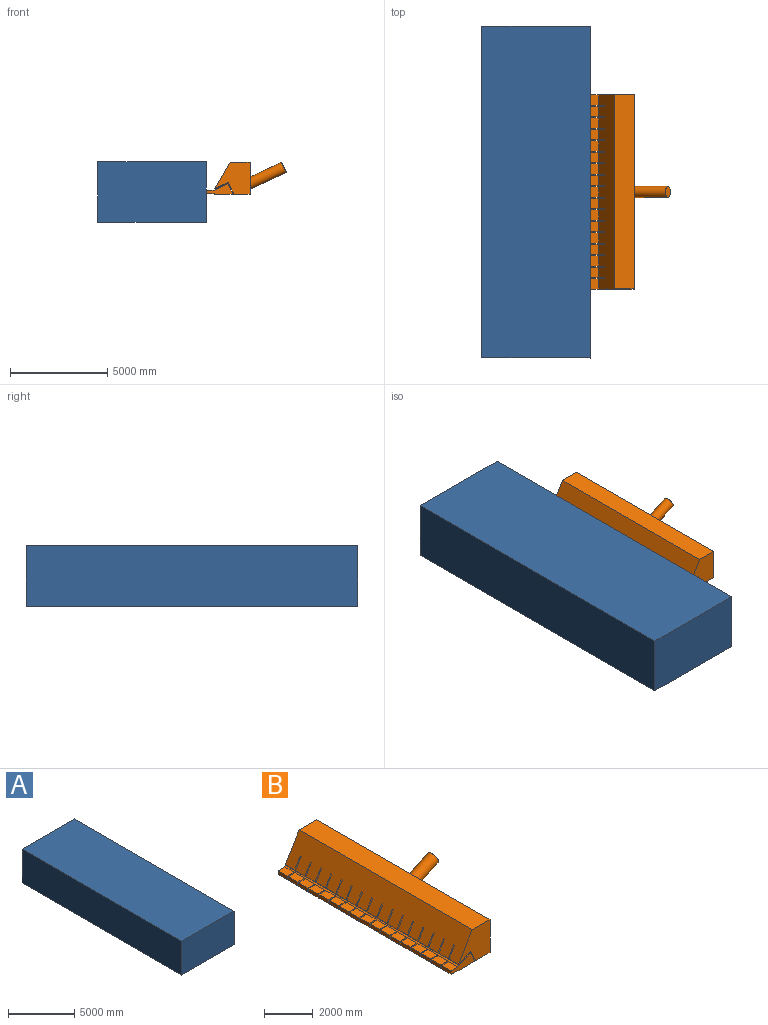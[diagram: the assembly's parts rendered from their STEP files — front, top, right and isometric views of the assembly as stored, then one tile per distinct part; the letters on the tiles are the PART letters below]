
ASSEMBLY  parts=2 mates=1
PART A: 6 faces, bbox 5600x17102.8x3131.8 mm
  f0: plane 5600x3131.8mm, normal (0,1,0), area 17538052.5mm2, adj f1,f3,f4,f5
  f1: plane 17102.78x5600mm, normal (0,0,1), area 95775550.1mm2, adj f0,f2,f4,f5
  f2: plane 5600x3131.8mm, normal (0,-1,0), area 17538052.5mm2, adj f1,f3,f4,f5
  f3: plane 17102.78x5600mm, normal (0,0,-1), area 95775550.1mm2, adj f0,f2,f4,f5
  f4: plane 17102.78x3131.8mm, normal (1,0,0), area 53562392.3mm2, adj f0,f1,f2,f3
  f5: plane 17102.78x3131.8mm, normal (-1,0,0), area 53562392.3mm2, adj f0,f1,f2,f3
PART B: 333 faces, bbox 4166.6x10055.9x1705.6 mm
  f0: plane 540x397.5mm, normal (0,0,1), area 214650.5mm2, adj f16,f38,f85,f86
  f1: plane 540x397.5mm, normal (0,0,1), area 214650.5mm2, adj f17,f38,f82,f83
  f2: plane 540x397.5mm, normal (0,0,1), area 214650.5mm2, adj f18,f38,f79,f80
  f3: plane 540x397.5mm, normal (0,0,1), area 214650.5mm2, adj f19,f38,f76,f77
  f4: plane 540x397.5mm, normal (0,0,1), area 214650.5mm2, adj f20,f38,f73,f74
  f5: plane 540x397.5mm, normal (0,0,1), area 214650.5mm2, adj f21,f38,f70,f71
  f6: plane 540x397.5mm, normal (0,0,1), area 214650.5mm2, adj f22,f38,f55,f68
  f7: plane 540x397.5mm, normal (0,0,1), area 214650.5mm2, adj f23,f38,f64,f65
  f8: plane 540x397.5mm, normal (0,0,1), area 214650.5mm2, adj f24,f38,f61,f62
  f9: plane 540x397.5mm, normal (0,0,1), area 214650.5mm2, adj f25,f38,f58,f59
  f10: plane 540x397.5mm, normal (0,0,1), area 214650.5mm2, adj f26,f38,f46,f56
  f11: plane 540x397.5mm, normal (0,0,1), area 214650.5mm2, adj f27,f38,f42,f53
  f12: plane 540x397.5mm, normal (0,0,1), area 214650.5mm2, adj f28,f38,f39,f50
  f13: plane 540x397.5mm, normal (0,0,1), area 214650.5mm2, adj f29,f38,f47,f52
  f14: plane 540x397.5mm, normal (0,0,1), area 214650.5mm2, adj f30,f38,f44,f49
  f15: plane 540x397.5mm, normal (0,0,1), area 214650.5mm2, adj f31,f38,f43,f67
  f16: plane 540x180.58mm, normal (-1,0,0), area 97510.9mm2, adj f0,f32,f85,f86
  f17: plane 540x180.58mm, normal (-1,0,0), area 97510.9mm2, adj f1,f32,f82,f83
  f18: plane 540x180.58mm, normal (-1,0,0), area 97510.9mm2, adj f2,f32,f79,f80
  f19: plane 540x180.58mm, normal (-1,0,0), area 97510.9mm2, adj f3,f32,f76,f77
  f20: plane 540x180.58mm, normal (-1,0,0), area 97510.9mm2, adj f4,f32,f73,f74
  f21: plane 540x180.58mm, normal (-1,0,0), area 97510.9mm2, adj f5,f32,f70,f71
  f22: plane 540x180.58mm, normal (-1,0,0), area 97510.9mm2, adj f6,f32,f55,f68
  f23: plane 540x180.58mm, normal (-1,0,0), area 97510.9mm2, adj f7,f32,f64,f65
  f24: plane 540x180.58mm, normal (-1,0,0), area 97510.9mm2, adj f8,f32,f61,f62
  f25: plane 540x180.58mm, normal (-1,0,0), area 97510.9mm2, adj f9,f32,f58,f59
  f26: plane 540x180.58mm, normal (-1,0,0), area 97510.9mm2, adj f10,f32,f46,f56
  f27: plane 540x180.58mm, normal (-1,0,0), area 97510.9mm2, adj f11,f32,f42,f53
  f28: plane 540x180.58mm, normal (-1,0,0), area 97510.9mm2, adj f12,f32,f39,f50
  f29: plane 540x180.58mm, normal (-1,0,0), area 97510.9mm2, adj f13,f32,f47,f52
  f30: plane 540x180.58mm, normal (-1,0,0), area 97510.9mm2, adj f14,f32,f44,f49
  f31: plane 540x180.58mm, normal (-1,0,0), area 97510.9mm2, adj f15,f32,f43,f67
  f32: plane 10000x398.52mm, normal (0,0,-1), area 3659198.5mm2, adj f16,f17,f18,f19,f20,f21,f22,f23
  f33: plane 540x397.5mm, normal (0,0,1), area 214650.5mm2, adj f34,f38,f40,f88
  f34: plane 540x180.58mm, normal (-1,0,0), area 97510.9mm2, adj f32,f33,f40,f88
  f35: plane 10000x24.82mm, normal (-1,0,0), area 248229.5mm2, adj f32,f36,f39,f40
  f36: plane 10000x976.6mm, normal (0,0,-1), area 9765991mm2, adj f35,f37,f39,f40
  f37: plane 10000x555.14mm, normal (0.89,0,0.45), area 6206617.3mm2, adj f36,f38,f39,f40
  f38: plane 10000x699.89mm, normal (-0.45,0,0.89), area 5947466.5mm2, adj f0,f1,f2,f3,f4,f5,f6,f7
  f39: plane 1375.12x555.14mm, normal (0,-1,0), area 414848.3mm2, adj f12,f28,f32,f35,f36,f37,f38
  f40: plane 1375.12x555.14mm, normal (0,1,0), area 414848.3mm2, adj f32,f33,f34,f35,f36,f37,f38
  f41: plane 180.37x51.25mm, normal (-1,0,0), area 9243.8mm2, adj f32,f38,f42,f43
  f42: plane 397.66x180.58mm, normal (0,-1,0), area 71742.9mm2, adj f11,f27,f32,f41
  f43: plane 397.66x180.58mm, normal (0,1,0), area 71742.9mm2, adj f15,f31,f32,f41
  f44: plane 397.66x180.58mm, normal (0,1,0), area 71742.9mm2, adj f14,f30,f32,f45
  f45: plane 180.37x51.25mm, normal (-1,0,0), area 9243.8mm2, adj f32,f38,f44,f46
  f46: plane 397.66x180.58mm, normal (0,-1,0), area 71742.9mm2, adj f10,f26,f32,f45
  f47: plane 397.66x180.58mm, normal (0,1,0), area 71742.9mm2, adj f13,f29,f32,f48
  f48: plane 180.37x51.25mm, normal (-1,0,0), area 9243.8mm2, adj f32,f38,f47,f49
  f49: plane 397.66x180.58mm, normal (0,-1,0), area 71742.9mm2, adj f14,f30,f32,f48
  f50: plane 397.66x180.58mm, normal (0,1,0), area 71742.9mm2, adj f12,f28,f32,f51
  f51: plane 180.37x51.25mm, normal (-1,0,0), area 9243.8mm2, adj f32,f38,f50,f52
  f52: plane 397.66x180.58mm, normal (0,-1,0), area 71742.9mm2, adj f13,f29,f32,f51
  f53: plane 397.66x180.58mm, normal (0,1,0), area 71742.9mm2, adj f11,f27,f32,f54
  f54: plane 180.37x51.25mm, normal (-1,0,0), area 9243.8mm2, adj f32,f38,f53,f55
  f55: plane 397.66x180.58mm, normal (0,-1,0), area 71742.9mm2, adj f6,f22,f32,f54
  f56: plane 397.66x180.58mm, normal (0,1,0), area 71742.9mm2, adj f10,f26,f32,f57
  f57: plane 180.37x51.25mm, normal (-1,0,0), area 9243.8mm2, adj f32,f38,f56,f58
  f58: plane 397.66x180.58mm, normal (0,-1,0), area 71742.9mm2, adj f9,f25,f32,f57
  f59: plane 397.66x180.58mm, normal (0,1,0), area 71742.9mm2, adj f9,f25,f32,f60
  f60: plane 180.37x51.25mm, normal (-1,0,0), area 9243.8mm2, adj f32,f38,f59,f61
  f61: plane 397.66x180.58mm, normal (0,-1,0), area 71742.9mm2, adj f8,f24,f32,f60
  f62: plane 397.66x180.58mm, normal (0,1,0), area 71742.9mm2, adj f8,f24,f32,f63
  f63: plane 180.37x51.25mm, normal (-1,0,0), area 9243.8mm2, adj f32,f38,f62,f64
  f64: plane 397.66x180.58mm, normal (0,-1,0), area 71742.9mm2, adj f7,f23,f32,f63
  f65: plane 397.66x180.58mm, normal (0,1,0), area 71742.9mm2, adj f7,f23,f32,f66
  f66: plane 180.37x51.25mm, normal (-1,0,0), area 9243.8mm2, adj f32,f38,f65,f67
  f67: plane 397.66x180.58mm, normal (0,-1,0), area 71742.9mm2, adj f15,f31,f32,f66
  f68: plane 397.66x180.58mm, normal (0,1,0), area 71742.9mm2, adj f6,f22,f32,f69
  f69: plane 180.37x51.25mm, normal (-1,0,0), area 9243.8mm2, adj f32,f38,f68,f70
  f70: plane 397.66x180.58mm, normal (0,-1,0), area 71742.9mm2, adj f5,f21,f32,f69
  f71: plane 397.66x180.58mm, normal (0,1,0), area 71742.9mm2, adj f5,f21,f32,f72
  f72: plane 180.37x51.25mm, normal (-1,0,0), area 9243.8mm2, adj f32,f38,f71,f73
  f73: plane 397.66x180.58mm, normal (0,-1,0), area 71742.9mm2, adj f4,f20,f32,f72
  f74: plane 397.66x180.58mm, normal (0,1,0), area 71742.9mm2, adj f4,f20,f32,f75
  f75: plane 180.37x51.25mm, normal (-1,0,0), area 9243.8mm2, adj f32,f38,f74,f76
  f76: plane 397.66x180.58mm, normal (0,-1,0), area 71742.9mm2, adj f3,f19,f32,f75
  f77: plane 397.66x180.58mm, normal (0,1,0), area 71742.9mm2, adj f3,f19,f32,f78
  f78: plane 180.37x51.25mm, normal (-1,0,0), area 9243.8mm2, adj f32,f38,f77,f79
  f79: plane 397.66x180.58mm, normal (0,-1,0), area 71742.9mm2, adj f2,f18,f32,f78
  f80: plane 397.66x180.58mm, normal (0,1,0), area 71742.9mm2, adj f2,f18,f32,f81
  f81: plane 180.37x51.25mm, normal (-1,0,0), area 9243.8mm2, adj f32,f38,f80,f82
  f82: plane 397.66x180.58mm, normal (0,-1,0), area 71742.9mm2, adj f1,f17,f32,f81
  f83: plane 397.66x180.58mm, normal (0,1,0), area 71742.9mm2, adj f1,f17,f32,f84
  f84: plane 180.37x51.25mm, normal (-1,0,0), area 9243.8mm2, adj f32,f38,f83,f85
  f85: plane 397.66x180.58mm, normal (0,-1,0), area 71742.9mm2, adj f0,f16,f32,f84
  f86: plane 397.66x180.58mm, normal (0,1,0), area 71742.9mm2, adj f0,f16,f32,f87
  f87: plane 180.37x51.25mm, normal (-1,0,0), area 9243.8mm2, adj f32,f38,f86,f88
  f88: plane 397.66x180.58mm, normal (0,-1,0), area 71742.9mm2, adj f32,f33,f34,f87
  f89: plane 540x25.23mm, normal (-0.93,0,-0.36), area 14632mm2, adj f105,f123,f131,f177
  f90: plane 540x25.23mm, normal (-0.93,0,-0.36), area 14632mm2, adj f106,f123,f169,f174
  f91: plane 540x25.23mm, normal (-0.93,0,-0.36), area 14632mm2, adj f107,f123,f166,f171
  f92: plane 540x25.23mm, normal (-0.93,0,-0.36), area 14632mm2, adj f108,f123,f163,f168
  f93: plane 540x25.23mm, normal (-0.93,0,-0.36), area 14632mm2, adj f109,f123,f160,f165
  f94: plane 540x25.23mm, normal (-0.93,0,-0.36), area 14632mm2, adj f110,f123,f157,f162
  f95: plane 540x25.23mm, normal (-0.93,0,-0.36), area 14632mm2, adj f111,f123,f154,f159
  f96: plane 540x25.23mm, normal (-0.93,0,-0.36), area 14632mm2, adj f112,f123,f151,f156
  f97: plane 540x25.23mm, normal (-0.93,0,-0.36), area 14632mm2, adj f113,f123,f129,f153
  f98: plane 540x25.23mm, normal (-0.93,0,-0.36), area 14632mm2, adj f114,f123,f150,f175
  f99: plane 540x25.23mm, normal (-0.93,0,-0.36), area 14632mm2, adj f115,f123,f147,f148
  f100: plane 540x25.23mm, normal (-0.93,0,-0.36), area 14632mm2, adj f116,f123,f144,f145
  f101: plane 540x25.23mm, normal (-0.93,0,-0.36), area 14632mm2, adj f117,f123,f141,f142
  f102: plane 540x25.23mm, normal (-0.93,0,-0.36), area 14632mm2, adj f118,f123,f138,f139
  f103: plane 540x25.23mm, normal (-0.93,0,-0.36), area 14632mm2, adj f119,f123,f135,f136
  f104: plane 540x25.23mm, normal (-0.93,0,-0.36), area 14632mm2, adj f120,f123,f132,f172
  f105: plane 684.4x540mm, normal (0.45,0,-0.89), area 302751.2mm2, adj f89,f126,f131,f177,f187,f188,f189,f190
  f106: plane 684.4x540mm, normal (0.45,0,-0.89), area 302751.2mm2, adj f90,f126,f169,f174,f257,f258,f259,f260
  f107: plane 684.4x540mm, normal (0.45,0,-0.89), area 302751.2mm2, adj f91,f126,f166,f171,f248,f249,f250,f251
  f108: plane 684.4x540mm, normal (0.45,0,-0.89), area 302751.2mm2, adj f92,f126,f163,f168,f239,f240,f241,f242
  f109: plane 684.4x540mm, normal (0.45,0,-0.89), area 302751.2mm2, adj f93,f126,f160,f165,f230,f231,f232,f233
  f110: plane 684.4x540mm, normal (0.45,0,-0.89), area 302751.2mm2, adj f94,f126,f157,f162,f221,f222,f223,f224
  f111: plane 684.4x540mm, normal (0.45,0,-0.89), area 302751.2mm2, adj f95,f126,f154,f159,f210,f213,f214,f215
  f112: plane 684.4x540mm, normal (0.45,0,-0.89), area 302751.2mm2, adj f96,f126,f151,f156,f203,f204,f205,f206
  f113: plane 684.4x540mm, normal (0.45,0,-0.89), area 302751.2mm2, adj f97,f126,f129,f153,f196,f197,f198,f199
  f114: plane 684.4x540mm, normal (0.45,0,-0.89), area 302751.2mm2, adj f98,f126,f150,f175,f266,f267,f268,f269
  f115: plane 684.4x540mm, normal (0.45,0,-0.89), area 302751.2mm2, adj f99,f126,f147,f148,f275,f276,f277,f278
  f116: plane 684.4x540mm, normal (0.45,0,-0.89), area 302751.2mm2, adj f100,f126,f144,f145,f284,f285,f286,f287
  f117: plane 684.4x540mm, normal (0.45,0,-0.89), area 302751.2mm2, adj f101,f126,f141,f142,f288,f294,f295,f296
  f118: plane 684.4x540mm, normal (0.45,0,-0.89), area 302751.2mm2, adj f102,f126,f138,f139,f302,f303,f304,f305
  f119: plane 684.4x540mm, normal (0.45,0,-0.89), area 302751.2mm2, adj f103,f126,f135,f136,f311,f312,f313,f314
  f120: plane 684.4x540mm, normal (0.45,0,-0.89), area 302751.2mm2, adj f104,f126,f132,f172,f178,f179,f180,f181
  f121: plane 10055.9x1700.9mm, normal (1,0,0), area 16168489.7mm2, adj f122,f127,f128,f129,f331
  f122: plane 10000x1029.08mm, normal (0,0,1), area 10290780.5mm2, adj f121,f123,f128,f129
  f123: plane 10000x1346.2mm, normal (-0.86,0,0.51), area 15132204mm2, adj f89,f90,f91,f92,f93,f94,f95,f96
  f124: plane 540x25.23mm, normal (-0.93,0,-0.36), area 14632mm2, adj f123,f125,f128,f133
  f125: plane 684.4x540mm, normal (0.45,0,-0.89), area 302751.2mm2, adj f124,f126,f128,f133,f320,f321,f322,f323
  f126: plane 10000x616.66mm, normal (-0.89,0,-0.45), area 6894431.3mm2, adj f105,f106,f107,f108,f109,f110,f111,f112
  f127: plane 10000x823.79mm, normal (0,0,-1), area 8237894.6mm2, adj f121,f126,f128,f129
  f128: plane 1826.39x1645.89mm, normal (0,-1,0), area 2066070.7mm2, adj f121,f122,f123,f124,f125,f126,f127
  f129: plane 1826.39x1645.89mm, normal (0,1,0), area 2066070.7mm2, adj f97,f113,f121,f122,f123,f126,f127
  f130: plane 375x222.1mm, normal (-0.51,0,-0.86), area 22336.6mm2, adj f123,f126,f131,f132
  f131: plane 694.27x564.3mm, normal (0,1,0), area 146854.6mm2, adj f89,f105,f123,f130
  f132: plane 694.27x564.3mm, normal (0,-1,0), area 146854.6mm2, adj f104,f120,f123,f130
  f133: plane 694.27x564.3mm, normal (0,1,0), area 146854.6mm2, adj f123,f124,f125,f134
  f134: plane 375x222.1mm, normal (-0.51,0,-0.86), area 22336.6mm2, adj f123,f126,f133,f135
  f135: plane 694.27x564.3mm, normal (0,-1,0), area 146854.6mm2, adj f103,f119,f123,f134
  f136: plane 694.27x564.3mm, normal (0,1,0), area 146854.6mm2, adj f103,f119,f123,f137
  f137: plane 375x222.1mm, normal (-0.51,0,-0.86), area 22336.6mm2, adj f123,f126,f136,f138
  f138: plane 694.27x564.3mm, normal (0,-1,0), area 146854.6mm2, adj f102,f118,f123,f137
  f139: plane 694.27x564.3mm, normal (0,1,0), area 146854.6mm2, adj f102,f118,f123,f140
  f140: plane 375x222.1mm, normal (-0.51,0,-0.86), area 22336.6mm2, adj f123,f126,f139,f141
  f141: plane 694.27x564.3mm, normal (0,-1,0), area 146854.6mm2, adj f101,f117,f123,f140
  f142: plane 694.27x564.3mm, normal (0,1,0), area 146854.6mm2, adj f101,f117,f123,f143
  f143: plane 375x222.1mm, normal (-0.51,0,-0.86), area 22336.6mm2, adj f123,f126,f142,f144
  f144: plane 694.27x564.3mm, normal (0,-1,0), area 146854.6mm2, adj f100,f116,f123,f143
  f145: plane 694.27x564.3mm, normal (0,1,0), area 146854.6mm2, adj f100,f116,f123,f146
  f146: plane 375x222.1mm, normal (-0.51,0,-0.86), area 22336.6mm2, adj f123,f126,f145,f147
  f147: plane 694.27x564.3mm, normal (0,-1,0), area 146854.6mm2, adj f99,f115,f123,f146
  f148: plane 694.27x564.3mm, normal (0,1,0), area 146854.6mm2, adj f99,f115,f123,f149
  f149: plane 375x222.1mm, normal (-0.51,0,-0.86), area 22336.6mm2, adj f123,f126,f148,f150
  f150: plane 694.27x564.3mm, normal (0,-1,0), area 146854.6mm2, adj f98,f114,f123,f149
  f151: plane 694.27x564.3mm, normal (0,1,0), area 146854.6mm2, adj f96,f112,f123,f152
  f152: plane 375x222.1mm, normal (-0.51,0,-0.86), area 22336.6mm2, adj f123,f126,f151,f153
  f153: plane 694.27x564.3mm, normal (0,-1,0), area 146854.6mm2, adj f97,f113,f123,f152
  f154: plane 694.27x564.3mm, normal (0,1,0), area 146854.6mm2, adj f95,f111,f123,f155
  f155: plane 375x222.1mm, normal (-0.51,0,-0.86), area 22336.6mm2, adj f123,f126,f154,f156
  f156: plane 694.27x564.3mm, normal (0,-1,0), area 146854.6mm2, adj f96,f112,f123,f155
  f157: plane 694.27x564.3mm, normal (0,1,0), area 146854.6mm2, adj f94,f110,f123,f158
  f158: plane 375x222.1mm, normal (-0.51,0,-0.86), area 22336.6mm2, adj f123,f126,f157,f159
  f159: plane 694.27x564.3mm, normal (0,-1,0), area 146854.6mm2, adj f95,f111,f123,f158
  f160: plane 694.27x564.3mm, normal (0,1,0), area 146854.6mm2, adj f93,f109,f123,f161
  f161: plane 375x222.1mm, normal (-0.51,0,-0.86), area 22336.6mm2, adj f123,f126,f160,f162
  f162: plane 694.27x564.3mm, normal (0,-1,0), area 146854.6mm2, adj f94,f110,f123,f161
  f163: plane 694.27x564.3mm, normal (0,1,0), area 146854.6mm2, adj f92,f108,f123,f164
  f164: plane 375x222.1mm, normal (-0.51,0,-0.86), area 22336.6mm2, adj f123,f126,f163,f165
  f165: plane 694.27x564.3mm, normal (0,-1,0), area 146854.6mm2, adj f93,f109,f123,f164
  f166: plane 694.27x564.3mm, normal (0,1,0), area 146854.6mm2, adj f91,f107,f123,f167
  f167: plane 375x222.1mm, normal (-0.51,0,-0.86), area 22336.6mm2, adj f123,f126,f166,f168
  f168: plane 694.27x564.3mm, normal (0,-1,0), area 146854.6mm2, adj f92,f108,f123,f167
  f169: plane 694.27x564.3mm, normal (0,1,0), area 146854.6mm2, adj f90,f106,f123,f170
  f170: plane 375x222.1mm, normal (-0.51,0,-0.86), area 22336.6mm2, adj f123,f126,f169,f171
  f171: plane 694.27x564.3mm, normal (0,-1,0), area 146854.6mm2, adj f91,f107,f123,f170
  f172: plane 694.27x564.3mm, normal (0,1,0), area 146854.6mm2, adj f104,f120,f123,f173
  f173: plane 375x222.1mm, normal (-0.51,0,-0.86), area 22336.6mm2, adj f123,f126,f172,f174
  f174: plane 694.27x564.3mm, normal (0,-1,0), area 146854.6mm2, adj f90,f106,f123,f173
  f175: plane 694.27x564.3mm, normal (0,1,0), area 146854.6mm2, adj f98,f114,f123,f176
  f176: plane 375x222.1mm, normal (-0.51,0,-0.86), area 22336.6mm2, adj f123,f126,f175,f177
  f177: plane 694.27x564.3mm, normal (0,-1,0), area 146854.6mm2, adj f89,f105,f123,f176
  f178: cylinder r=62.5mm len=132.32mm, axis (0.45,0,-0.89), area 18015.8mm2, adj f38,f120
  f179: cylinder r=62.5mm len=132.32mm, axis (0.45,0,-0.89), area 18015.8mm2, adj f38,f120
  f180: cylinder r=62.5mm len=132.32mm, axis (0.45,0,-0.89), area 18015.8mm2, adj f38,f120
  f181: cylinder r=62.5mm len=132.32mm, axis (0.45,0,-0.89), area 18015.8mm2, adj f38,f120
  f182: cylinder r=62.5mm len=132.32mm, axis (0.45,0,-0.89), area 18015.8mm2, adj f38,f120
  f183: cylinder r=62.5mm len=132.32mm, axis (0.45,0,-0.89), area 18015.8mm2, adj f38,f120
  f184: cylinder r=62.5mm len=132.32mm, axis (0.45,0,-0.89), area 18015.8mm2, adj f38,f120
  f185: cylinder r=62.5mm len=132.32mm, axis (0.45,0,-0.89), area 18015.8mm2, adj f38,f120
  f186: cylinder r=62.5mm len=132.32mm, axis (0.45,0,-0.89), area 18015.8mm2, adj f38,f120
  f187: cylinder r=62.5mm len=132.32mm, axis (0.45,0,-0.89), area 18015.8mm2, adj f38,f105
  f188: cylinder r=62.5mm len=132.32mm, axis (0.45,0,-0.89), area 18015.8mm2, adj f38,f105
  f189: cylinder r=62.5mm len=132.32mm, axis (0.45,0,-0.89), area 18015.8mm2, adj f38,f105
  f190: cylinder r=62.5mm len=132.32mm, axis (0.45,0,-0.89), area 18015.8mm2, adj f38,f105
  f191: cylinder r=62.5mm len=132.32mm, axis (0.45,0,-0.89), area 18015.8mm2, adj f38,f105
  f192: cylinder r=62.5mm len=132.32mm, axis (0.45,0,-0.89), area 18015.8mm2, adj f38,f105
  f193: cylinder r=62.5mm len=132.32mm, axis (0.45,0,-0.89), area 18015.8mm2, adj f38,f105
  f194: cylinder r=62.5mm len=132.32mm, axis (0.45,0,-0.89), area 18015.8mm2, adj f38,f105
  f195: cylinder r=62.5mm len=132.32mm, axis (0.45,0,-0.89), area 18015.8mm2, adj f38,f105
  f196: cylinder r=62.5mm len=132.32mm, axis (0.45,0,-0.89), area 18015.8mm2, adj f38,f113
  f197: cylinder r=62.5mm len=132.32mm, axis (0.45,0,-0.89), area 18015.8mm2, adj f38,f113
  f198: cylinder r=62.5mm len=132.32mm, axis (0.45,0,-0.89), area 18015.8mm2, adj f38,f113
  f199: cylinder r=62.5mm len=132.32mm, axis (0.45,0,-0.89), area 18015.8mm2, adj f38,f113
  f200: cylinder r=62.5mm len=132.32mm, axis (0.45,0,-0.89), area 18015.8mm2, adj f38,f113
  f201: cylinder r=62.5mm len=132.32mm, axis (0.45,0,-0.89), area 18015.8mm2, adj f38,f113
  f202: cylinder r=62.5mm len=132.32mm, axis (0.45,0,-0.89), area 18015.8mm2, adj f38,f113
  f203: cylinder r=62.5mm len=132.32mm, axis (0.45,0,-0.89), area 18015.8mm2, adj f38,f112
  f204: cylinder r=62.5mm len=132.32mm, axis (0.45,0,-0.89), area 18015.8mm2, adj f38,f112
  f205: cylinder r=62.5mm len=132.32mm, axis (0.45,0,-0.89), area 18015.8mm2, adj f38,f112
  f206: cylinder r=62.5mm len=132.32mm, axis (0.45,0,-0.89), area 18015.8mm2, adj f38,f112
  f207: cylinder r=62.5mm len=132.32mm, axis (0.45,0,-0.89), area 18015.8mm2, adj f38,f112
  f208: cylinder r=62.5mm len=132.32mm, axis (0.45,0,-0.89), area 18015.8mm2, adj f38,f112
  f209: cylinder r=62.5mm len=132.32mm, axis (0.45,0,-0.89), area 18015.8mm2, adj f38,f112
  f210: cylinder r=62.5mm len=132.32mm, axis (0.45,0,-0.89), area 18015.8mm2, adj f38,f111
  f211: cylinder r=62.5mm len=132.32mm, axis (0.45,0,-0.89), area 18015.8mm2, adj f38,f112
  f212: cylinder r=62.5mm len=132.32mm, axis (0.45,0,-0.89), area 18015.8mm2, adj f38,f112
  f213: cylinder r=62.5mm len=132.32mm, axis (0.45,0,-0.89), area 18015.8mm2, adj f38,f111
  f214: cylinder r=62.5mm len=132.32mm, axis (0.45,0,-0.89), area 18015.8mm2, adj f38,f111
  f215: cylinder r=62.5mm len=132.32mm, axis (0.45,0,-0.89), area 18015.8mm2, adj f38,f111
  f216: cylinder r=62.5mm len=132.32mm, axis (0.45,0,-0.89), area 18015.8mm2, adj f38,f111
  f217: cylinder r=62.5mm len=132.32mm, axis (0.45,0,-0.89), area 18015.8mm2, adj f38,f111
  f218: cylinder r=62.5mm len=132.32mm, axis (0.45,0,-0.89), area 18015.8mm2, adj f38,f111
  f219: cylinder r=62.5mm len=132.32mm, axis (0.45,0,-0.89), area 18015.8mm2, adj f38,f111
  f220: cylinder r=62.5mm len=132.32mm, axis (0.45,0,-0.89), area 18015.8mm2, adj f38,f111
  f221: cylinder r=62.5mm len=132.32mm, axis (0.45,0,-0.89), area 18015.8mm2, adj f38,f110
  f222: cylinder r=62.5mm len=132.32mm, axis (0.45,0,-0.89), area 18015.8mm2, adj f38,f110
  f223: cylinder r=62.5mm len=132.32mm, axis (0.45,0,-0.89), area 18015.8mm2, adj f38,f110
  f224: cylinder r=62.5mm len=132.32mm, axis (0.45,0,-0.89), area 18015.8mm2, adj f38,f110
  f225: cylinder r=62.5mm len=132.32mm, axis (0.45,0,-0.89), area 18015.8mm2, adj f38,f110
  f226: cylinder r=62.5mm len=132.32mm, axis (0.45,0,-0.89), area 18015.8mm2, adj f38,f110
  f227: cylinder r=62.5mm len=132.32mm, axis (0.45,0,-0.89), area 18015.8mm2, adj f38,f110
  f228: cylinder r=62.5mm len=132.32mm, axis (0.45,0,-0.89), area 18015.8mm2, adj f38,f110
  f229: cylinder r=62.5mm len=132.32mm, axis (0.45,0,-0.89), area 18015.8mm2, adj f38,f110
  f230: cylinder r=62.5mm len=132.32mm, axis (0.45,0,-0.89), area 18015.8mm2, adj f38,f109
  f231: cylinder r=62.5mm len=132.32mm, axis (0.45,0,-0.89), area 18015.8mm2, adj f38,f109
  f232: cylinder r=62.5mm len=132.32mm, axis (0.45,0,-0.89), area 18015.8mm2, adj f38,f109
  f233: cylinder r=62.5mm len=132.32mm, axis (0.45,0,-0.89), area 18015.8mm2, adj f38,f109
  f234: cylinder r=62.5mm len=132.32mm, axis (0.45,0,-0.89), area 18015.8mm2, adj f38,f109
  f235: cylinder r=62.5mm len=132.32mm, axis (0.45,0,-0.89), area 18015.8mm2, adj f38,f109
  f236: cylinder r=62.5mm len=132.32mm, axis (0.45,0,-0.89), area 18015.8mm2, adj f38,f109
  f237: cylinder r=62.5mm len=132.32mm, axis (0.45,0,-0.89), area 18015.8mm2, adj f38,f109
  f238: cylinder r=62.5mm len=132.32mm, axis (0.45,0,-0.89), area 18015.8mm2, adj f38,f109
  f239: cylinder r=62.5mm len=132.32mm, axis (0.45,0,-0.89), area 18015.8mm2, adj f38,f108
  f240: cylinder r=62.5mm len=132.32mm, axis (0.45,0,-0.89), area 18015.8mm2, adj f38,f108
  f241: cylinder r=62.5mm len=132.32mm, axis (0.45,0,-0.89), area 18015.8mm2, adj f38,f108
  f242: cylinder r=62.5mm len=132.32mm, axis (0.45,0,-0.89), area 18015.8mm2, adj f38,f108
  f243: cylinder r=62.5mm len=132.32mm, axis (0.45,0,-0.89), area 18015.8mm2, adj f38,f108
  f244: cylinder r=62.5mm len=132.32mm, axis (0.45,0,-0.89), area 18015.8mm2, adj f38,f108
  f245: cylinder r=62.5mm len=132.32mm, axis (0.45,0,-0.89), area 18015.8mm2, adj f38,f108
  f246: cylinder r=62.5mm len=132.32mm, axis (0.45,0,-0.89), area 18015.8mm2, adj f38,f108
  f247: cylinder r=62.5mm len=132.32mm, axis (0.45,0,-0.89), area 18015.8mm2, adj f38,f108
  f248: cylinder r=62.5mm len=132.32mm, axis (0.45,0,-0.89), area 18015.8mm2, adj f38,f107
  f249: cylinder r=62.5mm len=132.32mm, axis (0.45,0,-0.89), area 18015.8mm2, adj f38,f107
  f250: cylinder r=62.5mm len=132.32mm, axis (0.45,0,-0.89), area 18015.8mm2, adj f38,f107
  f251: cylinder r=62.5mm len=132.32mm, axis (0.45,0,-0.89), area 18015.8mm2, adj f38,f107
  f252: cylinder r=62.5mm len=132.32mm, axis (0.45,0,-0.89), area 18015.8mm2, adj f38,f107
  f253: cylinder r=62.5mm len=132.32mm, axis (0.45,0,-0.89), area 18015.8mm2, adj f38,f107
  f254: cylinder r=62.5mm len=132.32mm, axis (0.45,0,-0.89), area 18015.8mm2, adj f38,f107
  f255: cylinder r=62.5mm len=132.32mm, axis (0.45,0,-0.89), area 18015.8mm2, adj f38,f107
  f256: cylinder r=62.5mm len=132.32mm, axis (0.45,0,-0.89), area 18015.8mm2, adj f38,f107
  f257: cylinder r=62.5mm len=132.32mm, axis (0.45,0,-0.89), area 18015.8mm2, adj f38,f106
  f258: cylinder r=62.5mm len=132.32mm, axis (0.45,0,-0.89), area 18015.8mm2, adj f38,f106
  f259: cylinder r=62.5mm len=132.32mm, axis (0.45,0,-0.89), area 18015.8mm2, adj f38,f106
  f260: cylinder r=62.5mm len=132.32mm, axis (0.45,0,-0.89), area 18015.8mm2, adj f38,f106
  f261: cylinder r=62.5mm len=132.32mm, axis (0.45,0,-0.89), area 18015.8mm2, adj f38,f106
  f262: cylinder r=62.5mm len=132.32mm, axis (0.45,0,-0.89), area 18015.8mm2, adj f38,f106
  f263: cylinder r=62.5mm len=132.32mm, axis (0.45,0,-0.89), area 18015.8mm2, adj f38,f106
  f264: cylinder r=62.5mm len=132.32mm, axis (0.45,0,-0.89), area 18015.8mm2, adj f38,f106
  f265: cylinder r=62.5mm len=132.32mm, axis (0.45,0,-0.89), area 18015.8mm2, adj f38,f106
  f266: cylinder r=62.5mm len=132.32mm, axis (0.45,0,-0.89), area 18015.8mm2, adj f38,f114
  f267: cylinder r=62.5mm len=132.32mm, axis (0.45,0,-0.89), area 18015.8mm2, adj f38,f114
  f268: cylinder r=62.5mm len=132.32mm, axis (0.45,0,-0.89), area 18015.8mm2, adj f38,f114
  f269: cylinder r=62.5mm len=132.32mm, axis (0.45,0,-0.89), area 18015.8mm2, adj f38,f114
  f270: cylinder r=62.5mm len=132.32mm, axis (0.45,0,-0.89), area 18015.8mm2, adj f38,f114
  f271: cylinder r=62.5mm len=132.32mm, axis (0.45,0,-0.89), area 18015.8mm2, adj f38,f114
  f272: cylinder r=62.5mm len=132.32mm, axis (0.45,0,-0.89), area 18015.8mm2, adj f38,f114
  f273: cylinder r=62.5mm len=132.32mm, axis (0.45,0,-0.89), area 18015.8mm2, adj f38,f114
  f274: cylinder r=62.5mm len=132.32mm, axis (0.45,0,-0.89), area 18015.8mm2, adj f38,f114
  f275: cylinder r=62.5mm len=132.32mm, axis (0.45,0,-0.89), area 18015.8mm2, adj f38,f115
  f276: cylinder r=62.5mm len=132.32mm, axis (0.45,0,-0.89), area 18015.8mm2, adj f38,f115
  f277: cylinder r=62.5mm len=132.32mm, axis (0.45,0,-0.89), area 18015.8mm2, adj f38,f115
  f278: cylinder r=62.5mm len=132.32mm, axis (0.45,0,-0.89), area 18015.8mm2, adj f38,f115
  f279: cylinder r=62.5mm len=132.32mm, axis (0.45,0,-0.89), area 18015.8mm2, adj f38,f115
  f280: cylinder r=62.5mm len=132.32mm, axis (0.45,0,-0.89), area 18015.8mm2, adj f38,f115
  f281: cylinder r=62.5mm len=132.32mm, axis (0.45,0,-0.89), area 18015.8mm2, adj f38,f115
  f282: cylinder r=62.5mm len=132.32mm, axis (0.45,0,-0.89), area 18015.8mm2, adj f38,f115
  f283: cylinder r=62.5mm len=132.32mm, axis (0.45,0,-0.89), area 18015.8mm2, adj f38,f115
  f284: cylinder r=62.5mm len=132.32mm, axis (0.45,0,-0.89), area 18015.8mm2, adj f38,f116
  f285: cylinder r=62.5mm len=132.32mm, axis (0.45,0,-0.89), area 18015.8mm2, adj f38,f116
  f286: cylinder r=62.5mm len=132.32mm, axis (0.45,0,-0.89), area 18015.8mm2, adj f38,f116
  f287: cylinder r=62.5mm len=132.32mm, axis (0.45,0,-0.89), area 18015.8mm2, adj f38,f116
  f288: cylinder r=62.5mm len=132.32mm, axis (0.45,0,-0.89), area 18015.8mm2, adj f38,f117
  f289: cylinder r=62.5mm len=132.32mm, axis (0.45,0,-0.89), area 18015.8mm2, adj f38,f116
  f290: cylinder r=62.5mm len=132.32mm, axis (0.45,0,-0.89), area 18015.8mm2, adj f38,f116
  f291: cylinder r=62.5mm len=132.32mm, axis (0.45,0,-0.89), area 18015.8mm2, adj f38,f116
  f292: cylinder r=62.5mm len=132.32mm, axis (0.45,0,-0.89), area 18015.8mm2, adj f38,f116
  f293: cylinder r=62.5mm len=132.32mm, axis (0.45,0,-0.89), area 18015.8mm2, adj f38,f116
  f294: cylinder r=62.5mm len=132.32mm, axis (0.45,0,-0.89), area 18015.8mm2, adj f38,f117
  f295: cylinder r=62.5mm len=132.32mm, axis (0.45,0,-0.89), area 18015.8mm2, adj f38,f117
  f296: cylinder r=62.5mm len=132.32mm, axis (0.45,0,-0.89), area 18015.8mm2, adj f38,f117
  f297: cylinder r=62.5mm len=132.32mm, axis (0.45,0,-0.89), area 18015.8mm2, adj f38,f117
  f298: cylinder r=62.5mm len=132.32mm, axis (0.45,0,-0.89), area 18015.8mm2, adj f38,f117
  f299: cylinder r=62.5mm len=132.32mm, axis (0.45,0,-0.89), area 18015.8mm2, adj f38,f117
  f300: cylinder r=62.5mm len=132.32mm, axis (0.45,0,-0.89), area 18015.8mm2, adj f38,f117
  f301: cylinder r=62.5mm len=132.32mm, axis (0.45,0,-0.89), area 18015.8mm2, adj f38,f117
  f302: cylinder r=62.5mm len=132.32mm, axis (0.45,0,-0.89), area 18015.8mm2, adj f38,f118
  f303: cylinder r=62.5mm len=132.32mm, axis (0.45,0,-0.89), area 18015.8mm2, adj f38,f118
  f304: cylinder r=62.5mm len=132.32mm, axis (0.45,0,-0.89), area 18015.8mm2, adj f38,f118
  f305: cylinder r=62.5mm len=132.32mm, axis (0.45,0,-0.89), area 18015.8mm2, adj f38,f118
  f306: cylinder r=62.5mm len=132.32mm, axis (0.45,0,-0.89), area 18015.8mm2, adj f38,f118
  f307: cylinder r=62.5mm len=132.32mm, axis (0.45,0,-0.89), area 18015.8mm2, adj f38,f118
  f308: cylinder r=62.5mm len=132.32mm, axis (0.45,0,-0.89), area 18015.8mm2, adj f38,f118
  f309: cylinder r=62.5mm len=132.32mm, axis (0.45,0,-0.89), area 18015.8mm2, adj f38,f118
  f310: cylinder r=62.5mm len=132.32mm, axis (0.45,0,-0.89), area 18015.8mm2, adj f38,f118
  f311: cylinder r=62.5mm len=132.32mm, axis (0.45,0,-0.89), area 18015.8mm2, adj f38,f119
  f312: cylinder r=62.5mm len=132.32mm, axis (0.45,0,-0.89), area 18015.8mm2, adj f38,f119
  f313: cylinder r=62.5mm len=132.32mm, axis (0.45,0,-0.89), area 18015.8mm2, adj f38,f119
  f314: cylinder r=62.5mm len=132.32mm, axis (0.45,0,-0.89), area 18015.8mm2, adj f38,f119
  f315: cylinder r=62.5mm len=132.32mm, axis (0.45,0,-0.89), area 18015.8mm2, adj f38,f119
  f316: cylinder r=62.5mm len=132.32mm, axis (0.45,0,-0.89), area 18015.8mm2, adj f38,f119
  f317: cylinder r=62.5mm len=132.32mm, axis (0.45,0,-0.89), area 18015.8mm2, adj f38,f119
  f318: cylinder r=62.5mm len=132.32mm, axis (0.45,0,-0.89), area 18015.8mm2, adj f38,f119
  f319: cylinder r=62.5mm len=132.32mm, axis (0.45,0,-0.89), area 18015.8mm2, adj f38,f119
  f320: cylinder r=62.5mm len=132.32mm, axis (0.45,0,-0.89), area 18015.8mm2, adj f38,f125
  f321: cylinder r=62.5mm len=132.32mm, axis (0.45,0,-0.89), area 18015.8mm2, adj f38,f125
  f322: cylinder r=62.5mm len=132.32mm, axis (0.45,0,-0.89), area 18015.8mm2, adj f38,f125
  f323: cylinder r=62.5mm len=132.32mm, axis (0.45,0,-0.89), area 18015.8mm2, adj f38,f125
  f324: cylinder r=62.5mm len=132.32mm, axis (0.45,0,-0.89), area 18015.8mm2, adj f38,f125
  f325: cylinder r=62.5mm len=132.32mm, axis (0.45,0,-0.89), area 18015.8mm2, adj f38,f125
  f326: cylinder r=62.5mm len=132.32mm, axis (0.45,0,-0.89), area 18015.8mm2, adj f38,f125
  f327: cylinder r=62.5mm len=132.32mm, axis (0.45,0,-0.89), area 18015.8mm2, adj f38,f125
  f328: cylinder r=62.5mm len=132.32mm, axis (0.45,0,-0.89), area 18015.8mm2, adj f38,f125
  f329: cylinder r=62.5mm len=132.32mm, axis (0.45,0,-0.89), area 18015.8mm2, adj f38,f113
  f330: cylinder r=62.5mm len=132.32mm, axis (0.45,0,-0.89), area 18015.8mm2, adj f38,f113
  f331: cylinder r=285mm len=2101.45mm, axis (-0.91,0,-0.42), area 3438159mm2, adj f121,f332
  f332: plane 570x516.6mm, normal (0.91,0,0.42), area 255175.9mm2, adj f331
PLACE A rot(axis=(0,1,0),0deg) t=(-4848.02,0,-3.32)mm
PLACE B at identity
MATE fastened A.f4 <-> B.f27  axis (1,0,0) through (-2048.64,0,-724.89)mm
